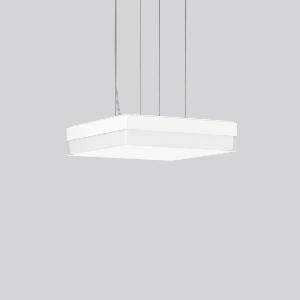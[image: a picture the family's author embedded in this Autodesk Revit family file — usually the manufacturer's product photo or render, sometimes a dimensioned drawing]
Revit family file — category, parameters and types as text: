
# Revit family: flat_slim_square_312542_002_76_79b6
name_source: partatom
category: Lighting Fixtures
units: mm (PartAtom-declared; Revit-internal decimal feet)

## family parameters
Cut with Voids When Loaded = No
Host = Face
Light Source = No
Part Type = Normal
Room Calculation Point = No
Round Connector Dimension = Use Diameter
Shared = No

## types (1)
- MultiLumen 2 840 (1 x LED Modul 840, 2300 lm, 4000)
    Apparent Load = 21 VA
    CIE Flux Codes = 43 75 93 91 100
    Color Rendering = 80
    Color Temperature = 4000
    Default Elevation = 1800 mm
    Height = 70 mm
    Lamp = 1 x LED Modul 840
    Lamp Light Flux = 2300 lm
    Lamp count = 1
    Length = 300 mm
    Lifetime = 50000 h
    Luminous efficacy = 110 lm/W
    Manufacturer = RZB
    ModVariant = No
    Model = 312542.002.76
    Mounting Place = Ceiling
    Mounting Type = Pendant
    Number of Poles = 1
    OnlyDefault = Yes
    Power Factor = 1
    Product Name = FLAT SLIM square
    Product group = Pendant luminaires
    ProductGroupID = 902
    Protection Class = Protection class I
    Protection Degree = IP 40
    RLX_Detail_Level = 1
    RLX_Emergency_Light_Flux = 0 lm
    RLX_Emergency_Type = 0
    RLX_Emergency_Type_DB = No
    RlxData = <blob elided: 13661 chars, md5=30dfdf0d>
    Socket = socket
    Standby Power = 0 W
    System Light Flux = 2300 lm
    System Power = 21 W
    Type Comments = MultiLumen 2 840
    Type Image = 312542.002.jpg
    URL = http://relux.com
    VarID = multilumen_2_840
    Voltage = 230 V
    Voltage Range = 220-240 V
    Weight = 0.00 kg
    Width = 300 mm

## geometry (parser evidence)
native form markers: Sweep x12
no freeform markers — native parametric forms only
